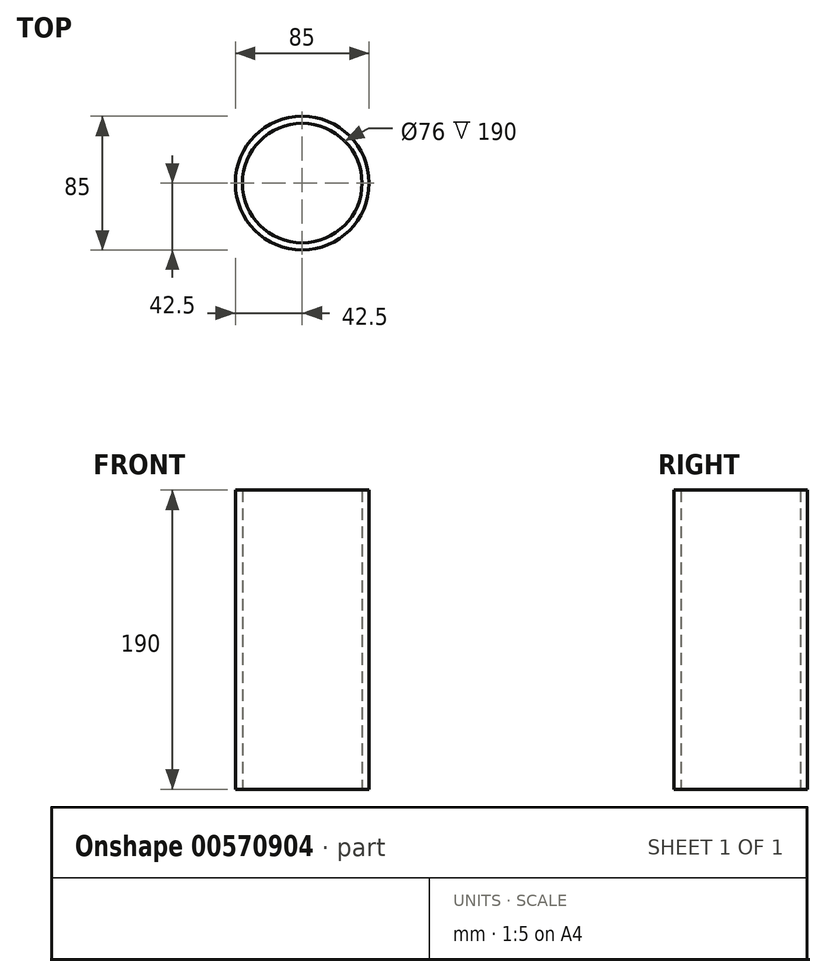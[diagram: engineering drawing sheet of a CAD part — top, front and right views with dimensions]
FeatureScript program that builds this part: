
annotation { "Feature Type Name" : "Feature", "Feature Type Description" : "" }
export const myFeature = defineFeature(function(context is Context, id is Id, definition is map)
    precondition{}
    {
        {
            var Q0;
            Q0=qCreatedBy(makeId("Top.planeOp"),FACE);
            var sketch = newSketch(context, id + "F0", { "sketchPlane" : qUnion([Q0])});
            skCircle(sketch, "E0", {"center": v(0, 0) * mm, "radius": 38 * mm});
            skCircle(sketch, "E1", {"center": v(0, 0) * mm, "radius": 42.5 * mm});
            skSolve(sketch);
        }
        {
            var Q0;
            Q0 = qSketchRegion(id + "F0", true);
            extrude(context, id + "F1", {"entities" : qUnion([Q0]), "depth" : 190 * mm, "offsetDistance" : 25 * mm});
        }
    });
